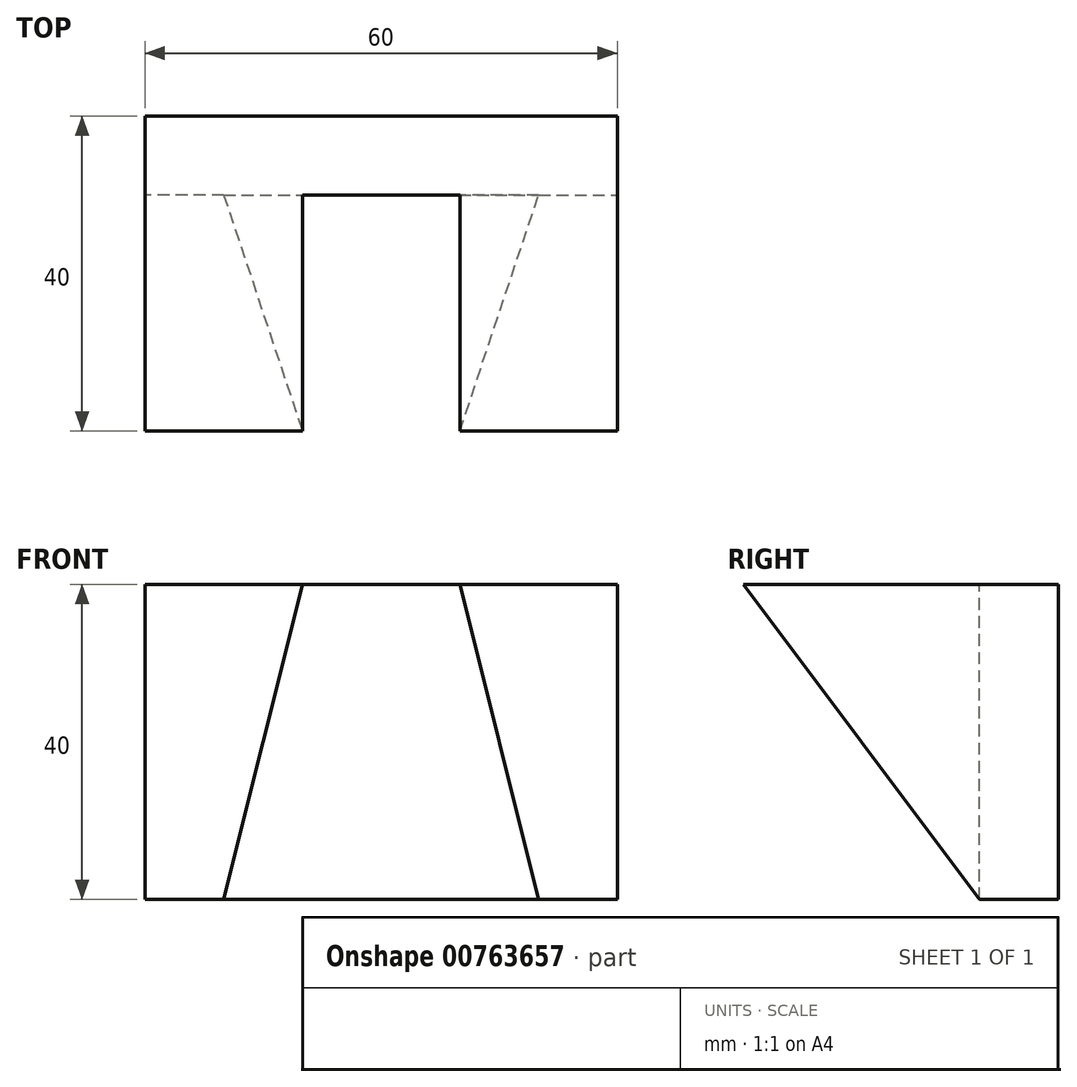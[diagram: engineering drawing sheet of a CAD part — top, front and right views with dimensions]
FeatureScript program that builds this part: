
annotation { "Feature Type Name" : "Feature", "Feature Type Description" : "" }
export const myFeature = defineFeature(function(context is Context, id is Id, definition is map)
    precondition{}
    {
        {
            var Q0;
            Q0=qCreatedBy(makeId("Front.planeOp"),FACE);
            var sketch = newSketch(context, id + "F0", { "sketchPlane" : qUnion([Q0])});
            skLineSegment(sketch, "E0.bottom", {"start": v(-41.25, 46.2) * mm, "end": v(18.75, 46.2) * mm});
            skLineSegment(sketch, "E0.top", {"start": v(-41.25, 6.2) * mm, "end": v(18.75, 6.2) * mm});
            skLineSegment(sketch, "E0.left", {"start": v(-41.25, 46.2) * mm, "end": v(-41.25, 6.2) * mm});
            skLineSegment(sketch, "E0.right", {"start": v(18.75, 46.2) * mm, "end": v(18.75, 6.2) * mm});
            skLineSegment(sketch, "E1.bottom", {"start": v(-41.25, 46.2) * mm, "end": v(-21.25, 46.2) * mm});
            skLineSegment(sketch, "E1.top", {"start": v(-41.25, 46.2) * mm, "end": v(-21.25, 46.2) * mm});
            skLineSegment(sketch, "E1.left", {"start": v(-41.25, 46.2) * mm, "end": v(-41.25, 46.2) * mm});
            skLineSegment(sketch, "E1.right", {"start": v(-21.25, 46.2) * mm, "end": v(-21.25, 46.2) * mm});
            skLineSegment(sketch, "E2", {"start": v(-41.25, 6.2) * mm, "end": v(-31.25, 6.2) * mm});
            skLineSegment(sketch, "E3", {"start": v(-31.25, 6.2) * mm, "end": v(-21.25, 6.2) * mm});
            skLineSegment(sketch, "E4", {"start": v(-21.25, 6.2) * mm, "end": v(-11.25, 6.2) * mm});
            skLineSegment(sketch, "E5", {"start": v(-11.25, 6.2) * mm, "end": v(-1.25, 6.2) * mm});
            skLineSegment(sketch, "E6", {"start": v(-1.25, 6.2) * mm, "end": v(8.75, 6.2) * mm});
            skLineSegment(sketch, "E7", {"start": v(8.75, 6.2) * mm, "end": v(18.75, 6.2) * mm});
            skLineSegment(sketch, "E8", {"start": v(-21.25, 46.2) * mm, "end": v(-31.25, 6.2) * mm});
            skLineSegment(sketch, "E9", {"start": v(18.75, 46.2) * mm, "end": v(-1.25, 46.2) * mm});
            skLineSegment(sketch, "E10", {"start": v(-1.25, 46.2) * mm, "end": v(8.75, 6.2) * mm});
            skSolve(sketch);
        }
        {
            var Q0;
            Q0=makeQuery(id+"F0.imprint","IMPRINT",FACE,{"disambiguationData":[TD([[makeQuery(id+"F0.imprint","IMPRINT",EDGE,{"derivedFrom":sQuery(id+"F0.wireOp",EDGE,"E0.bottom")}),-1.0]])]});
            extrude(context, id + "F1", {"entities" : qUnion([Q0]), "depth" : 10 * mm, "offsetDistance" : 25 * mm});
        }
        {
            var Q0;
            Q0=makeQuery(id+"F0.imprint","IMPRINT",FACE,{"disambiguationData":[TD([[makeQuery(id+"F0.imprint","IMPRINT",EDGE,{"derivedFrom":sQuery(id+"F0.wireOp",EDGE,"E0.left")}),1.0]])]});
            extrude(context, id + "F2", {"entities" : qUnion([Q0]), "operationType" : NewBodyOperationType.ADD, "depth" : 40 * mm, "offsetDistance" : 25 * mm});
        }
        {
            var Q0;
            Q0=makeQuery(id+"F0.imprint","IMPRINT",FACE,{"disambiguationData":[TD([[makeQuery(id+"F0.imprint","IMPRINT",EDGE,{"derivedFrom":sQuery(id+"F0.wireOp",EDGE,"E0.right")}),-1.0]])]});
            extrude(context, id + "F3", {"entities" : qUnion([Q0]), "operationType" : NewBodyOperationType.ADD, "depth" : 40 * mm, "offsetDistance" : 25 * mm});
        }
        {
            var Q0;
            Q0=makeQuery(id+"F2.opExtrude","SWEPT_FACE",FACE,{"disambiguationData":[OSD([sQuery(id+"F0.wireOp",EDGE,"E0.left")])]});
            var sketch = newSketch(context, id + "F4", { "sketchPlane" : qUnion([Q0])});
            skLineSegment(sketch, "E11", {"start": v(0, 6.2) * mm, "end": v(10, 6.2) * mm});
            skLineSegment(sketch, "E12", {"start": v(10, 6.2) * mm, "end": v(20, 6.2) * mm});
            skLineSegment(sketch, "E13", {"start": v(20, 6.2) * mm, "end": v(30, 6.2) * mm});
            skLineSegment(sketch, "E14", {"start": v(30, 6.2) * mm, "end": v(40, 6.2) * mm});
            skLineSegment(sketch, "E15", {"start": v(40, 46.2) * mm, "end": v(20, 6.2) * mm});
            skSolve(sketch);
        }
        {
            var Q0;
            Q0=makeQuery(id+"F4.imprint","IMPRINT",FACE,{"disambiguationData":[TD([[makeQuery(id+"F4.imprint","IMPRINT",EDGE,{"derivedFrom":sQuery(id+"F4.wireOp",EDGE,"E13")}),-1.0]])]});
            extrude(context, id + "F5", {"entities" : qUnion([Q0]), "operationType" : NewBodyOperationType.REMOVE, "oppositeDirection" : true, "depth" : 25 * mm, "offsetDistance" : 25 * mm});
        }
        {
            var Q0;
            Q0=makeQuery(id+"F3.opExtrude","SWEPT_FACE",FACE,{"disambiguationData":[OSD([sQuery(id+"F0.wireOp",EDGE,"E0.right")])]});
            var sketch = newSketch(context, id + "F6", { "sketchPlane" : qUnion([Q0])});
            skLineSegment(sketch, "E16", {"start": v(0, 6.2) * mm, "end": v(-10, 6.2) * mm});
            skLineSegment(sketch, "E17", {"start": v(-10, 6.2) * mm, "end": v(-20, 6.2) * mm});
            skLineSegment(sketch, "E18", {"start": v(-20, 6.2) * mm, "end": v(-30, 6.2) * mm});
            skLineSegment(sketch, "E19", {"start": v(-30, 6.2) * mm, "end": v(-40, 6.2) * mm});
            skLineSegment(sketch, "E20", {"start": v(-40, 46.2) * mm, "end": v(-20, 6.2) * mm});
            skSolve(sketch);
        }
        {
            var Q0;
            Q0=makeQuery(id+"F6.imprint","IMPRINT",FACE,{"disambiguationData":[TD([[makeQuery(id+"F6.imprint","IMPRINT",EDGE,{"derivedFrom":sQuery(id+"F6.wireOp",EDGE,"E18")}),1.0]])]});
            extrude(context, id + "F7", {"entities" : qUnion([Q0]), "operationType" : NewBodyOperationType.REMOVE, "oppositeDirection" : true, "depth" : 25 * mm, "offsetDistance" : 25 * mm});
        }
        {
            var Q0;
            Q0=makeQuery(id+"F2.opExtrude","SWEPT_FACE",FACE,{"disambiguationData":[OSD([sQuery(id+"F0.wireOp",EDGE,"E0.left")])]});
            var sketch = newSketch(context, id + "F8", { "sketchPlane" : qUnion([Q0])});
            skLineSegment(sketch, "E21", {"start": v(40, 46.2) * mm, "end": v(10, 6.2) * mm});
            skSolve(sketch);
        }
        {
            var Q0;
            {var subQ0=sQuery(id+"F8.wireOp",EDGE,"E21");Q0=makeQuery(id+"F8.imprint","IMPRINT",FACE,{"disambiguationData":[TD([[makeQuery(id+"F8.imprint","IMPRINT",EDGE,{"derivedFrom":subQ0}),1.0]])]});}
            extrude(context, id + "F9", {"entities" : qUnion([Q0]), "operationType" : NewBodyOperationType.REMOVE, "oppositeDirection" : true, "depth" : 25 * mm, "offsetDistance" : 25 * mm});
        }
        {
            var Q0;
            Q0=makeQuery(id+"F3.opExtrude","SWEPT_FACE",FACE,{"disambiguationData":[OSD([sQuery(id+"F0.wireOp",EDGE,"E0.right")])]});
            var sketch = newSketch(context, id + "F10", { "sketchPlane" : qUnion([Q0])});
            skLineSegment(sketch, "E22", {"start": v(-40, 46.2) * mm, "end": v(-10, 6.2) * mm});
            skSolve(sketch);
        }
        {
            var Q0;
            {var subQ0=sQuery(id+"F10.wireOp",EDGE,"E22");Q0=makeQuery(id+"F10.imprint","IMPRINT",FACE,{"disambiguationData":[TD([[makeQuery(id+"F10.imprint","IMPRINT",EDGE,{"derivedFrom":subQ0}),-1.0]])]});}
            extrude(context, id + "F11", {"entities" : qUnion([Q0]), "operationType" : NewBodyOperationType.REMOVE, "oppositeDirection" : true, "depth" : 25 * mm, "offsetDistance" : 25 * mm});
        }
    });
